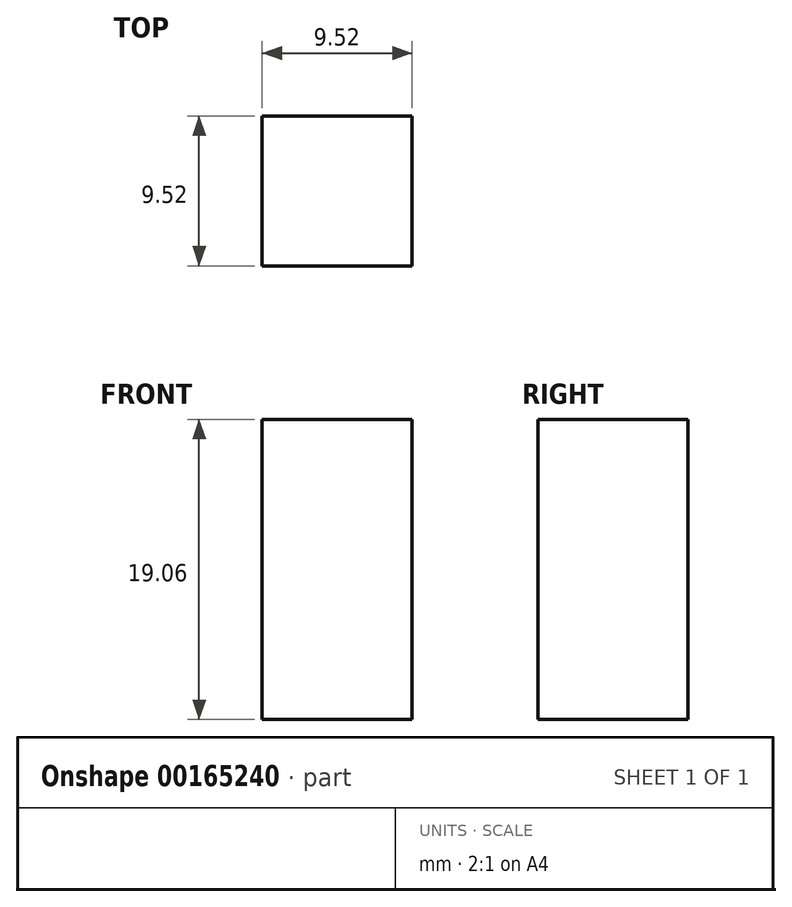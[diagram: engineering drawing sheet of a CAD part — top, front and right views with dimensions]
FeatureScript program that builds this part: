
annotation { "Feature Type Name" : "Feature", "Feature Type Description" : "" }
export const myFeature = defineFeature(function(context is Context, id is Id, definition is map)
    precondition{}
    {
        {
            var Q0;
            Q0=qCreatedBy(makeId("Top.planeOp"),FACE);
            var sketch = newSketch(context, id + "F0", { "sketchPlane" : qUnion([Q0])});
            skLineSegment(sketch, "E0.bottom", {"start": v(4.76, 4.76) * mm, "end": v(-4.76, 4.76) * mm});
            skLineSegment(sketch, "E0.top", {"start": v(4.76, -4.76) * mm, "end": v(-4.76, -4.76) * mm});
            skLineSegment(sketch, "E0.left", {"start": v(4.76, 4.76) * mm, "end": v(4.76, -4.76) * mm});
            skLineSegment(sketch, "E0.right", {"start": v(-4.76, 4.76) * mm, "end": v(-4.76, -4.76) * mm});
            skPoint(sketch, "E0.middle", {"position": v(0, 0) * mm});
            skSolve(sketch);
        }
        {
            var Q0;
            Q0=qSketchRegion(id+"F0",true);
            extrude(context, id + "F1", {"entities" : qUnion([Q0]), "depth" : 19.06 * mm});
        }
    });
